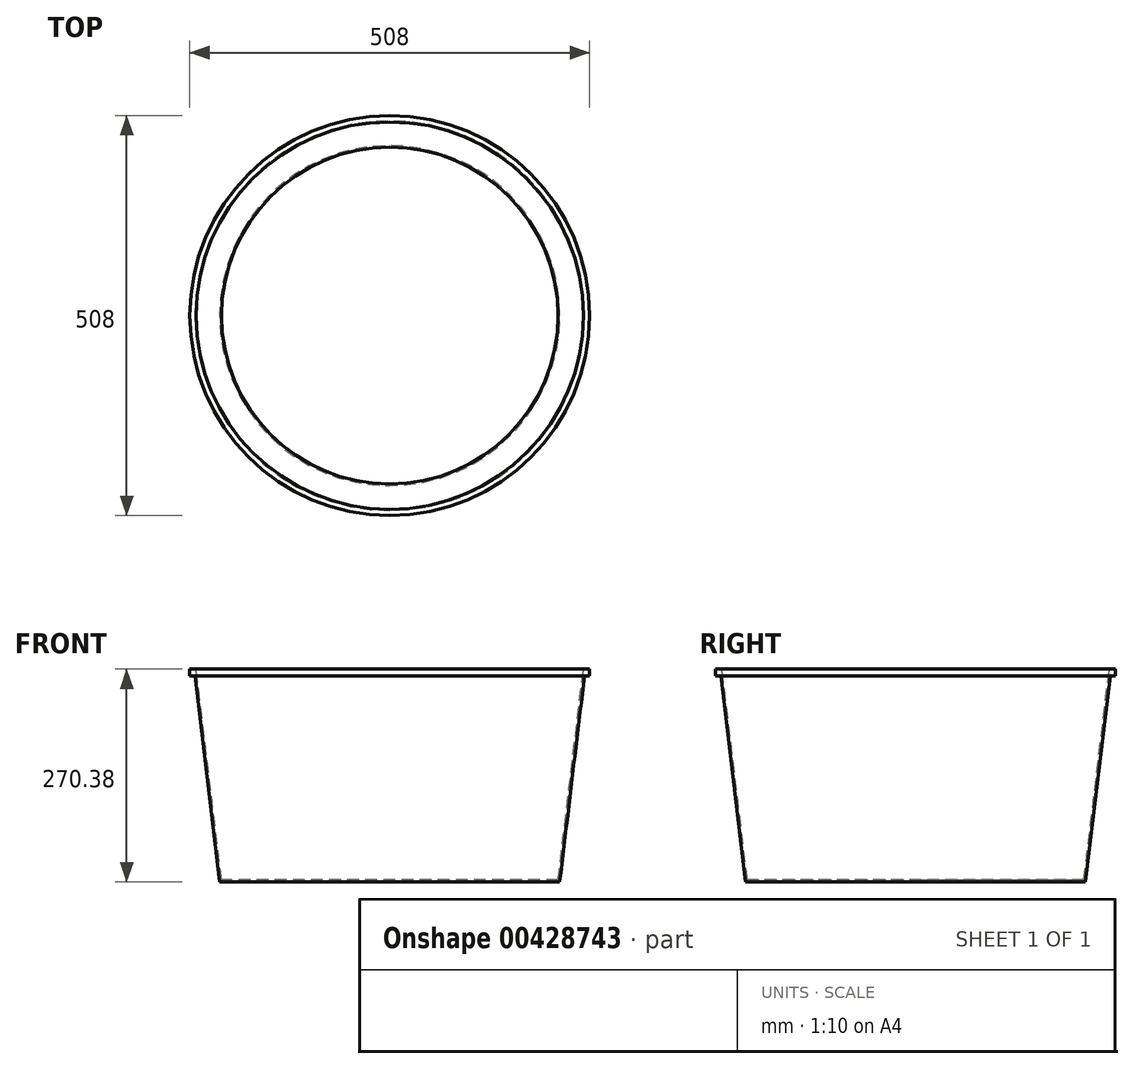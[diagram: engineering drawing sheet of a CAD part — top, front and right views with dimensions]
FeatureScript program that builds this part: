
annotation { "Feature Type Name" : "Feature", "Feature Type Description" : "" }
export const myFeature = defineFeature(function(context is Context, id is Id, definition is map)
    precondition{}
    {
        {
            var Q0;
            Q0=qCreatedBy(makeId("Front.planeOp"),FACE);
            var sketch = newSketch(context, id + "F0", { "sketchPlane" : qUnion([Q0])});
            skLineSegment(sketch, "E0", {"start": v(0, 0) * mm, "end": v(-215.9, 0) * mm});
            skLineSegment(sketch, "E1", {"start": v(-215.9, 0) * mm, "end": v(-247.32, 261.65) * mm});
            skLineSegment(sketch, "E2", {"start": v(-254, 261.65) * mm, "end": v(-247.32, 261.65) * mm});
            skLineSegment(sketch, "E3", {"start": v(0, 0) * mm, "end": v(0, 2.29) * mm});
            skLineSegment(sketch, "E4", {"start": v(0, 2.29) * mm, "end": v(-213.87, 2.29) * mm});
            skLineSegment(sketch, "E5", {"start": v(-213.87, 2.29) * mm, "end": v(-246.06, 270.38) * mm});
            skLineSegment(sketch, "E6", {"start": v(0, 169.52) * mm, "end": v(0, -110.98) * mm, "construction": true});
            skLineSegment(sketch, "E7", {"start": v(-254, 261.65) * mm, "end": v(-254, 270.38) * mm});
            skLineSegment(sketch, "E8", {"start": v(-254, 270.38) * mm, "end": v(-246.06, 270.38) * mm});
            skSolve(sketch);
        }
        {
            var Q0;
            Q0=makeQuery(id+"F0.imprint","IMPRINT",FACE,{"disambiguationData":[TD([[makeQuery(id+"F0.imprint","IMPRINT",EDGE,{"derivedFrom":sQuery(id+"F0.wireOp",EDGE,"E0")}),-1.0]])]});
            var Q1;
            Q1=sQuery(id+"F0.wireOp",EDGE,"E6");
            revolve(context, id + "F1", {"entities" : qUnion([Q0]), "axis" : qUnion([Q1]), "revolveType" : RevolveType.FULL});
        }
    });
